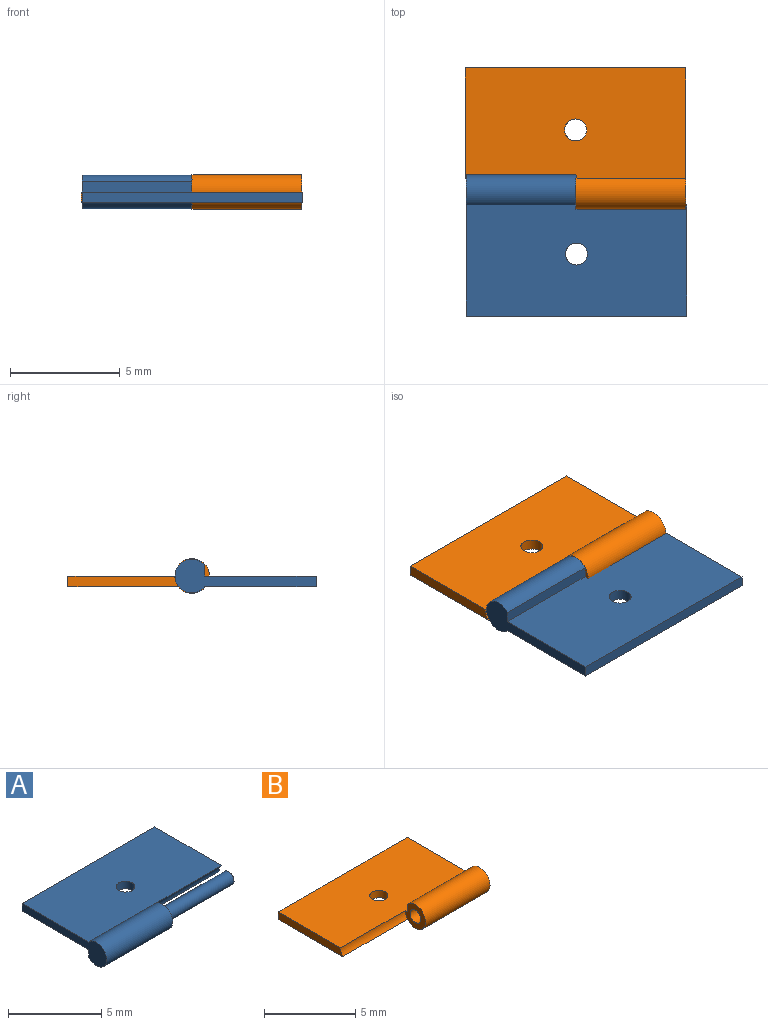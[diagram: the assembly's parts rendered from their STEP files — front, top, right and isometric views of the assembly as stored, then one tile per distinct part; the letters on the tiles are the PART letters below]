
ASSEMBLY  parts=2 mates=1
PART A: 12 faces, bbox 10x6.4x1.5 mm
  f0: plane 10.04x0.5mm, normal (0,1,0), area 5mm2, adj f1,f5,f6,f11
  f1: plane 6.41x1.53mm, normal (-1,0,0), area 4.3mm2, adj f0,f6,f7,f10,f11
  f2: cylinder r=0.77mm len=5.04mm, axis (-1,0,0), area 2.7mm2, adj f3,f5,f6,f11
  f3: plane 1.53x1.53mm, normal (1,0,0), area 1.3mm2, adj f2,f7,f8,f10,f11
  f4: cylinder r=0.5mm len=1mm, axis (0,0,1), area 1.6mm2, adj f6,f11
  f5: plane 5.06x0.5mm, normal (1,0,0), area 2.5mm2, adj f0,f2,f6,f11
  f6: plane 10.04x5.06mm, normal (0,0,1), area 50mm2, adj f0,f1,f2,f4,f5,f7
  f7: cylinder r=0.77mm len=5mm, axis (-1,0,0), area 18.6mm2, adj f1,f3,f6,f10
  f8: cylinder r=0.41mm len=5mm, axis (-1,0,0), area 12.8mm2, adj f3,f9
  f9: plane 0.81x0.81mm, normal (1,0,0), area 0.5mm2, adj f8
  f10: plane 5x0.5mm, normal (0,1,0), area 2.5mm2, adj f1,f3,f7,f11
  f11: plane 10.04x5.06mm, normal (0,0,-1), area 49.1mm2, adj f0,f1,f2,f3,f4,f5,f10
PART B: 11 faces, bbox 10x6.4x1.6 mm
  f0: plane 6.43x1.58mm, normal (1,0,0), area 3.8mm2, adj f1,f3,f5,f7,f9,f10
  f1: plane 10.04x0.5mm, normal (0,1,0), area 5mm2, adj f0,f2,f3,f10
  f2: plane 5.03x0.5mm, normal (-1,0,0), area 2.5mm2, adj f1,f3,f4,f10
  f3: plane 10.04x5.03mm, normal (0,0,-1), area 49.7mm2, adj f0,f1,f2,f4,f5,f8
  f4: cylinder r=0.79mm len=5.04mm, axis (1,0,0), area 2.7mm2, adj f2,f3,f6,f10
  f5: cylinder r=0.79mm len=5mm, axis (1,0,0), area 19.5mm2, adj f0,f3,f6,f9
  f6: plane 1.58x1.58mm, normal (-1,0,0), area 1.4mm2, adj f4,f5,f7,f9,f10
  f7: cylinder r=0.42mm len=5mm, axis (1,0,0), area 13.1mm2, adj f0,f6
  f8: cylinder r=0.5mm len=1mm, axis (0,0,1), area 1.6mm2, adj f3,f10
  f9: plane 5x0.5mm, normal (0,1,0), area 2.5mm2, adj f0,f5,f6,f10
  f10: plane 10.04x5.03mm, normal (0,0,1), area 48.8mm2, adj f0,f1,f2,f4,f6,f8,f9
PLACE A rot(axis=(1,0,0),180deg) t=(-33.69,-36.37,-16.97)mm
PLACE B t=(-33.72,-30.72,-17.97)mm fixed
MATE revolute B.f4 <-> A.f2  axis (1,0,0) through (-28.71,-33.54,-17.47)mm
